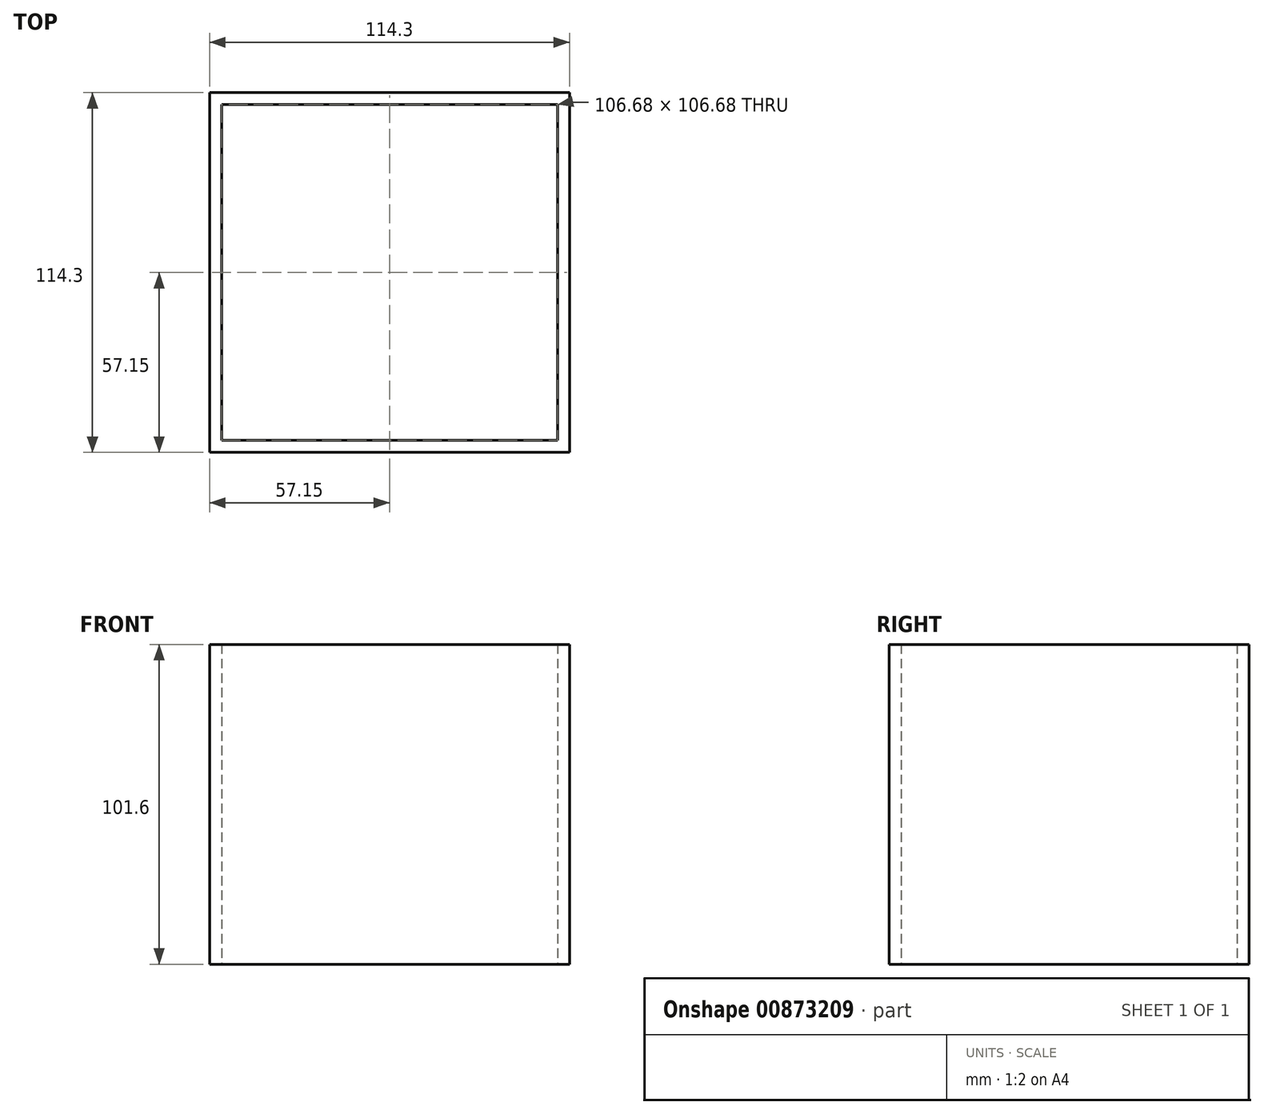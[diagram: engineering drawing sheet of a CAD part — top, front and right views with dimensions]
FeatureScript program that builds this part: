
annotation { "Feature Type Name" : "Feature", "Feature Type Description" : "" }
export const myFeature = defineFeature(function(context is Context, id is Id, definition is map)
    precondition{}
    {
        {
            var Q0;
            Q0=qCreatedBy(makeId("Front.planeOp"),FACE);
            var sketch = newSketch(context, id + "F0", { "sketchPlane" : qUnion([Q0])});
            skLineSegment(sketch, "E0.bottom", {"start": v(57.15, 50.8) * mm, "end": v(-57.15, 50.8) * mm});
            skLineSegment(sketch, "E0.top", {"start": v(57.15, -50.8) * mm, "end": v(-57.15, -50.8) * mm});
            skLineSegment(sketch, "E0.left", {"start": v(57.15, 50.8) * mm, "end": v(57.15, -50.8) * mm});
            skLineSegment(sketch, "E0.right", {"start": v(-57.15, 50.8) * mm, "end": v(-57.15, -50.8) * mm});
            skPoint(sketch, "E0.middle", {"position": v(0, 0) * mm});
            skSolve(sketch);
        }
        {
            var Q0;
            Q0 = qSketchRegion(id + "F0", true);
            var Q1;
            Q1 = qConstructionFilter(qBodyType(qCreatedBy(id + "F0" ,EDGE), BodyType.WIRE), ConstructionObject.NO);
            extrude(context, id + "F1", {"entities" : qUnion([Q0]), "surfaceOperationType" : NewSurfaceOperationType.ADD, "surfaceEntities" : qUnion([Q1]), "depth" : 114.3 * mm, "offsetDistance" : 25.4 * mm});
        }
        {
            var Q0;
            Q0=qCreatedBy(makeId("Top.planeOp"),FACE);
            var sketch = newSketch(context, id + "F2", { "sketchPlane" : qUnion([Q0])});
            skLineSegment(sketch, "E1.bottom", {"start": v(-53.34, -3.81) * mm, "end": v(53.34, -3.81) * mm});
            skLineSegment(sketch, "E1.top", {"start": v(-53.34, -110.5) * mm, "end": v(53.34, -110.5) * mm});
            skLineSegment(sketch, "E1.left", {"start": v(-53.34, -3.81) * mm, "end": v(-53.34, -110.5) * mm});
            skLineSegment(sketch, "E1.right", {"start": v(53.34, -3.8) * mm, "end": v(53.34, -110.5) * mm});
            skSolve(sketch);
        }
        {
            var Q0;
            Q0 = qSketchRegion(id + "F2", true);
            extrude(context, id + "F3", {"entities" : qUnion([Q0]), "operationType" : NewBodyOperationType.REMOVE, "endBound" : BoundingType.THROUGH_ALL, "depth" : 25.4 * mm, "offsetDistance" : 25.4 * mm});
        }
        {
            var Q0;
            Q0 = qSketchRegion(id + "F2", true);
            extrude(context, id + "F4", {"entities" : qUnion([Q0]), "operationType" : NewBodyOperationType.REMOVE, "endBound" : BoundingType.THROUGH_ALL, "oppositeDirection" : true, "depth" : 25.4 * mm, "offsetDistance" : 25.4 * mm});
        }
    });
